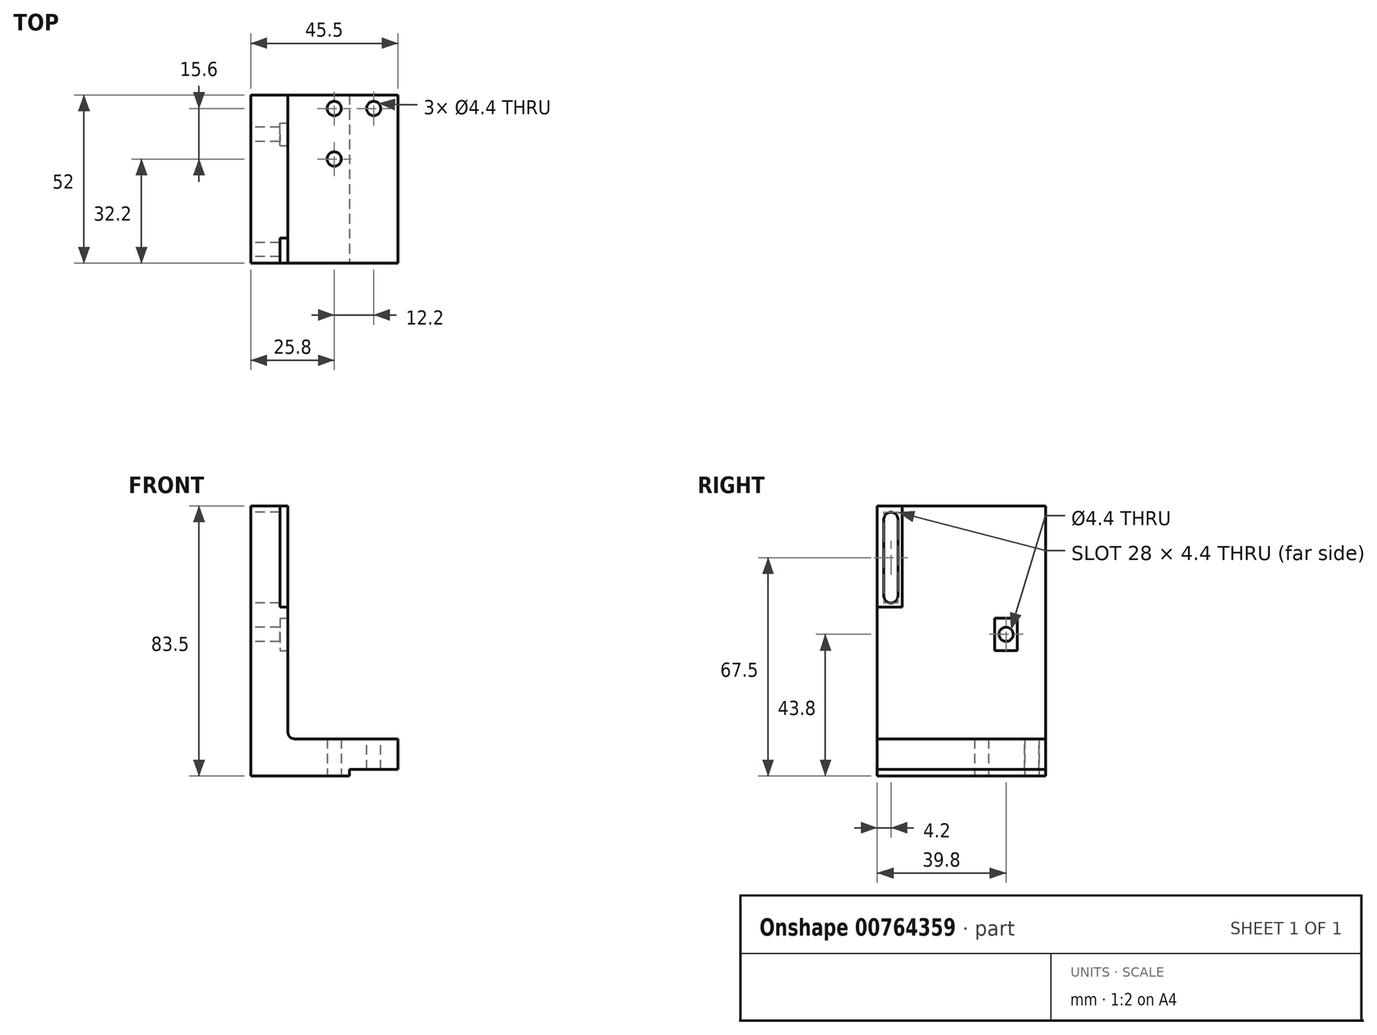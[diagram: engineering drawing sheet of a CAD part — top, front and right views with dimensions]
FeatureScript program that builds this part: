
annotation { "Feature Type Name" : "Feature", "Feature Type Description" : "" }
export const myFeature = defineFeature(function(context is Context, id is Id, definition is map)
    precondition{}
    {
        {
            var Q0;
            Q0=qCreatedBy(makeId("Front.planeOp"),FACE);
            var sketch = newSketch(context, id + "F0", { "sketchPlane" : qUnion([Q0])});
            skLineSegment(sketch, "E0.bottom", {"start": v(-11.5, 72) * mm, "end": v(34, 72) * mm});
            skLineSegment(sketch, "E0.top", {"start": v(-11.5, -11.5) * mm, "end": v(34, -11.5) * mm});
            skLineSegment(sketch, "E0.left", {"start": v(-11.5, 72) * mm, "end": v(-11.5, -11.5) * mm});
            skLineSegment(sketch, "E0.right", {"start": v(34, 72) * mm, "end": v(34, -11.5) * mm});
            skSolve(sketch);
        }
        {
            var Q0;
            Q0 = qSketchRegion(id + "F0", true);
            extrude(context, id + "F1", {"entities" : qUnion([Q0]), "depth" : 52 * mm, "offsetDistance" : 25 * mm});
        }
        {
            var Q0;
            Q0=makeQuery(id+"F1.opExtrude","CAP_FACE",FACE,{"disambiguationData":[OSD([sQuery(id+"F0.wireOp",EDGE,"E0.bottom"),sQuery(id+"F0.wireOp",EDGE,"E0.top"),sQuery(id+"F0.wireOp",EDGE,"E0.left"),sQuery(id+"F0.wireOp",EDGE,"E0.right")])],"isStart":false});
            var sketch = newSketch(context, id + "F2", { "sketchPlane" : qUnion([Q0])});
            skLineSegment(sketch, "E1.bottom", {"start": v(34, 72) * mm, "end": v(0, 72) * mm});
            skLineSegment(sketch, "E1.top", {"start": v(34, 0) * mm, "end": v(0, 0) * mm});
            skLineSegment(sketch, "E1.left", {"start": v(34, 72) * mm, "end": v(34, 0) * mm});
            skLineSegment(sketch, "E1.right", {"start": v(0, 72) * mm, "end": v(0, 0) * mm});
            skSolve(sketch);
        }
        {
            var Q0;
            Q0 = qSketchRegion(id + "F2", true);
            extrude(context, id + "F3", {"entities" : qUnion([Q0]), "operationType" : NewBodyOperationType.REMOVE, "endBound" : BoundingType.THROUGH_ALL, "oppositeDirection" : true, "depth" : 52 * mm, "offsetDistance" : 25 * mm});
        }
        {
            var Q0;
            Q0=makeQuery(id+"F1.opExtrude","SWEPT_FACE",FACE,{"disambiguationData":[OSD([sQuery(id+"F0.wireOp",EDGE,"E0.top")])]});
            var sketch = newSketch(context, id + "F4", { "sketchPlane" : qUnion([Q0])});
            skPoint(sketch, "E2", {"position": v(14.3, 4.2) * mm});
            skPoint(sketch, "E3", {"position": v(14.3, 19.8) * mm});
            skSolve(sketch);
        }
        {
            var Q0;
            Q0=makeQuery(id+"F1.opExtrude","CAP_FACE",FACE,{"disambiguationData":[OSD([sQuery(id+"F0.wireOp",EDGE,"E0.bottom"),sQuery(id+"F0.wireOp",EDGE,"E0.top"),sQuery(id+"F0.wireOp",EDGE,"E0.left"),sQuery(id+"F0.wireOp",EDGE,"E0.right")])],"isStart":false});
            var sketch = newSketch(context, id + "F5", { "sketchPlane" : qUnion([Q0])});
            skLineSegment(sketch, "E4.bottom", {"start": v(34, -11.5) * mm, "end": v(19, -11.5) * mm});
            skLineSegment(sketch, "E4.top", {"start": v(34, -9.5) * mm, "end": v(19, -9.5) * mm});
            skLineSegment(sketch, "E4.left", {"start": v(34, -11.5) * mm, "end": v(34, -9.5) * mm});
            skLineSegment(sketch, "E4.right", {"start": v(19, -11.5) * mm, "end": v(19, -9.5) * mm});
            skSolve(sketch);
        }
        {
            var Q0;
            Q0 = qSketchRegion(id + "F5", true);
            extrude(context, id + "F6", {"entities" : qUnion([Q0]), "operationType" : NewBodyOperationType.REMOVE, "endBound" : BoundingType.THROUGH_ALL, "oppositeDirection" : true, "depth" : 25 * mm, "offsetDistance" : 25 * mm});
        }
        {
            var Q0;
            Q0=makeQuery(id+"F3.boolean.opBoolean","COPY",FACE,{"derivedFrom":makeQuery(id+"F3.opExtrude","SWEPT_FACE",FACE,{"disambiguationData":[OSD([sQuery(id+"F2.wireOp",EDGE,"E1.top")])]})});
            var sketch = newSketch(context, id + "F7", { "sketchPlane" : qUnion([Q0])});
            skPoint(sketch, "E5", {"position": v(26.5, -4.2) * mm});
            skSolve(sketch);
        }
        {
            var Q0;
            Q0=makeQuery(id+"F3.boolean.opBoolean","COPY",EDGE,{"derivedFrom":makeQuery(id+"F3.opExtrude","SWEPT_EDGE",EDGE,{"disambiguationData":[OSD([sQuery(id+"F2.wireOp",EDGE,"E1.top"),sQuery(id+"F2.wireOp",EDGE,"E1.right")])]})});
            fillet(context, id + "F8", {"entities" : qUnion([Q0]), "radius" : 2 * mm, "tangentPropagation" : true, "allowEdgeOverflow" : false});
        }
        {
            var Q0;
            Q0=makeQuery(id+"F1.opExtrude","SWEPT_FACE",FACE,{"disambiguationData":[OSD([sQuery(id+"F0.wireOp",EDGE,"E0.left")])]});
            var sketch = newSketch(context, id + "F9", { "sketchPlane" : qUnion([Q0])});
            skPoint(sketch, "E6", {"position": v(12.2, 32.3) * mm});
            skSolve(sketch);
        }
        {
            var Q0;
            Q0=sQuery(id+"F7.wireOp",VERTEX,"E5");
            var Q1;
            Q1=sQuery(id+"F9.wireOp",VERTEX,"E6");
            var Q2;
            Q2=sQuery(id+"F4.wireOp",VERTEX,"9ac88c87-b674-4f94-b65b-44ee802f1d45");
            var Q3;
            Q3=sQuery(id+"F4.wireOp",VERTEX,"E3");
            var Q4;
            Q4=sQuery(id+"F4.wireOp",VERTEX,"E2");
            var Q5;
            Q5=makeQuery(id+"F1.opExtrude","SWEPT_BODY",BODY,{"disambiguationData":[OSD([sQuery(id+"F0.wireOp",EDGE,"E0.bottom"),sQuery(id+"F0.wireOp",EDGE,"E0.top"),sQuery(id+"F0.wireOp",EDGE,"E0.left"),sQuery(id+"F0.wireOp",EDGE,"E0.right")])]});
            hole(context, id + "F10", {"style" : HoleStyle.SIMPLE, "endStyle" : HoleEndStyle.THROUGH, "standardTappedOrClearance" : lookupTablePath({ "standard" : "ISO", "fit" : "Normal", "size" : "M4", "type" : "Clearance" }), "standardBlindInLast" : lookupTablePath({ "fit" : "Standard", "standard" : "ISO", "size" : "M4", "type" : "Clearance" }), "holeDiameter" : 4.4 * mm, "majorDiameter" : 5 * mm, "isTappedThrough" : true, "tappedDepth" : 12 * mm, "tapClearance" : 3, "locations" : qUnion([Q0, Q1, Q2, Q3, Q4]), "scope" : qUnion([Q5])});
        }
        {
            var Q0;
            Q0=makeQuery(id+"F1.opExtrude","SWEPT_FACE",FACE,{"disambiguationData":[OSD([sQuery(id+"F0.wireOp",EDGE,"E0.left")])]});
            var sketch = newSketch(context, id + "F11", { "sketchPlane" : qUnion([Q0])});
            skLineSegment(sketch, "E7.bottom", {"start": v(47.8, 70) * mm, "end": v(47.8, 70) * mm});
            skLineSegment(sketch, "E7.top", {"start": v(47.8, 42) * mm, "end": v(47.8, 42) * mm});
            skLineSegment(sketch, "E7.left", {"start": v(45.6, 67.8) * mm, "end": v(45.6, 44.2) * mm});
            skLineSegment(sketch, "E7.right", {"start": v(50, 67.8) * mm, "end": v(50, 44.2) * mm});
            skPoint(sketch, "E8.visualSharp", {"position": v(50, 70) * mm});
            skArc(sketch, "E8.filletArc", {"start": v(50, 67.8) * mm, "mid": v(49.36, 69.36) * mm, "end": v(47.8, 70) * mm});
            skPoint(sketch, "E9.visualSharp", {"position": v(45.6, 70) * mm});
            skArc(sketch, "E9.filletArc", {"start": v(47.8, 70) * mm, "mid": v(46.24, 69.36) * mm, "end": v(45.6, 67.8) * mm});
            skPoint(sketch, "E10.visualSharp", {"position": v(50, 42) * mm});
            skArc(sketch, "E10.filletArc", {"start": v(47.8, 42) * mm, "mid": v(49.36, 42.64) * mm, "end": v(50, 44.2) * mm});
            skPoint(sketch, "E11.visualSharp", {"position": v(45.6, 42) * mm});
            skArc(sketch, "E11.filletArc", {"start": v(45.6, 44.2) * mm, "mid": v(46.24, 42.64) * mm, "end": v(47.8, 42) * mm});
            skSolve(sketch);
        }
        {
            var Q0;
            Q0 = qSketchRegion(id + "F11", true);
            extrude(context, id + "F12", {"entities" : qUnion([Q0]), "operationType" : NewBodyOperationType.REMOVE, "endBound" : BoundingType.THROUGH_ALL, "oppositeDirection" : true, "depth" : 25 * mm, "offsetDistance" : 25 * mm});
        }
        {
            var Q0;
            Q0=makeQuery(id+"F3.boolean.opBoolean","COPY",FACE,{"derivedFrom":makeQuery(id+"F3.opExtrude","SWEPT_FACE",FACE,{"disambiguationData":[OSD([sQuery(id+"F2.wireOp",EDGE,"E1.right")])]})});
            var sketch = newSketch(context, id + "F13", { "sketchPlane" : qUnion([Q0])});
            skLineSegment(sketch, "E12.bottom", {"start": v(-15.7, 37.3) * mm, "end": v(-8.7, 37.3) * mm});
            skLineSegment(sketch, "E12.top", {"start": v(-15.7, 27.3) * mm, "end": v(-8.7, 27.3) * mm});
            skLineSegment(sketch, "E12.left", {"start": v(-15.7, 37.3) * mm, "end": v(-15.7, 27.3) * mm});
            skLineSegment(sketch, "E12.right", {"start": v(-8.7, 37.3) * mm, "end": v(-8.7, 27.3) * mm});
            skSolve(sketch);
        }
        {
            var Q0;
            Q0 = qSketchRegion(id + "F13", true);
            extrude(context, id + "F14", {"entities" : qUnion([Q0]), "operationType" : NewBodyOperationType.REMOVE, "oppositeDirection" : true, "depth" : 2.5 * mm, "offsetDistance" : 25 * mm});
        }
        {
            var Q0;
            Q0=makeQuery(id+"F3.boolean.opBoolean","COPY",FACE,{"derivedFrom":makeQuery(id+"F3.opExtrude","SWEPT_FACE",FACE,{"disambiguationData":[OSD([sQuery(id+"F2.wireOp",EDGE,"E1.right")])]})});
            var sketch = newSketch(context, id + "F15", { "sketchPlane" : qUnion([Q0])});
            skLineSegment(sketch, "E13.bottom", {"start": v(-52, 40.7) * mm, "end": v(-44.3, 40.7) * mm});
            skLineSegment(sketch, "E13.top", {"start": v(-52, 72) * mm, "end": v(-44.3, 72) * mm});
            skLineSegment(sketch, "E13.left", {"start": v(-44.3, 40.7) * mm, "end": v(-44.3, 72) * mm});
            skLineSegment(sketch, "E13.right", {"start": v(-52, 40.7) * mm, "end": v(-52, 72) * mm});
            skSolve(sketch);
        }
        {
            var Q0;
            Q0=makeQuery(id+"F15.imprint","IMPRINT",FACE,{"disambiguationData":[TD([[makeQuery(id+"F15.imprint","IMPRINT",EDGE,{"derivedFrom":sQuery(id+"F15.wireOp",EDGE,"E13.bottom")}),1.0]])]});
            extrude(context, id + "F16", {"entities" : qUnion([Q0]), "operationType" : NewBodyOperationType.REMOVE, "oppositeDirection" : true, "depth" : 2.5 * mm, "offsetDistance" : 25 * mm});
        }
    });
